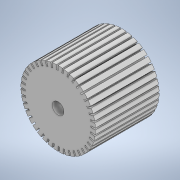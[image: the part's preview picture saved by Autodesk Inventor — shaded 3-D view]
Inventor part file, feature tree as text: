
AUTODESK INVENTOR PART (.ipt)
format: ipt  version: 2022 (Build 260153000, 153)  size: 307,712 bytes
history: native  units: mm
features: sketch x3, extrude x2, hole x1
ambient origin geometry x8: Origin, YZ Plane, XZ Plane, XY Plane, X Axis, Y Axis, Z Axis, Center Point
bodies: Solid1 (feature_tree)
feature tree (6):
  extrude  "Extrusion1"  Depth=32.639mm TaperAngle=0.0deg
  extrude  "Extrusion2"  Depth=0.745mm
  hole  "Hole1"  [1 undecoded]
  sketch  "Sketch1"  dims[d0=38.1mm d1=32.639mm d2=0.0mm]
  sketch  "Sketch2"  dims[d3=2.235mm d4=0.745mm]
  sketch  "Sketch3"  dims[d5=400.0mm d7=360.0deg d9=0.0mm d10=0.0mm d11=6.0mm d12=6.0mm d13=4.0mm d14=2.0mm d15=90.0deg d16=8.0mm d17=20.594885mm]
note: 1 required parameter value undecoded (feature->parameter linkage not recoverable at this tier; creation-order binding heuristic only, values carry confidence <= 0.55)
